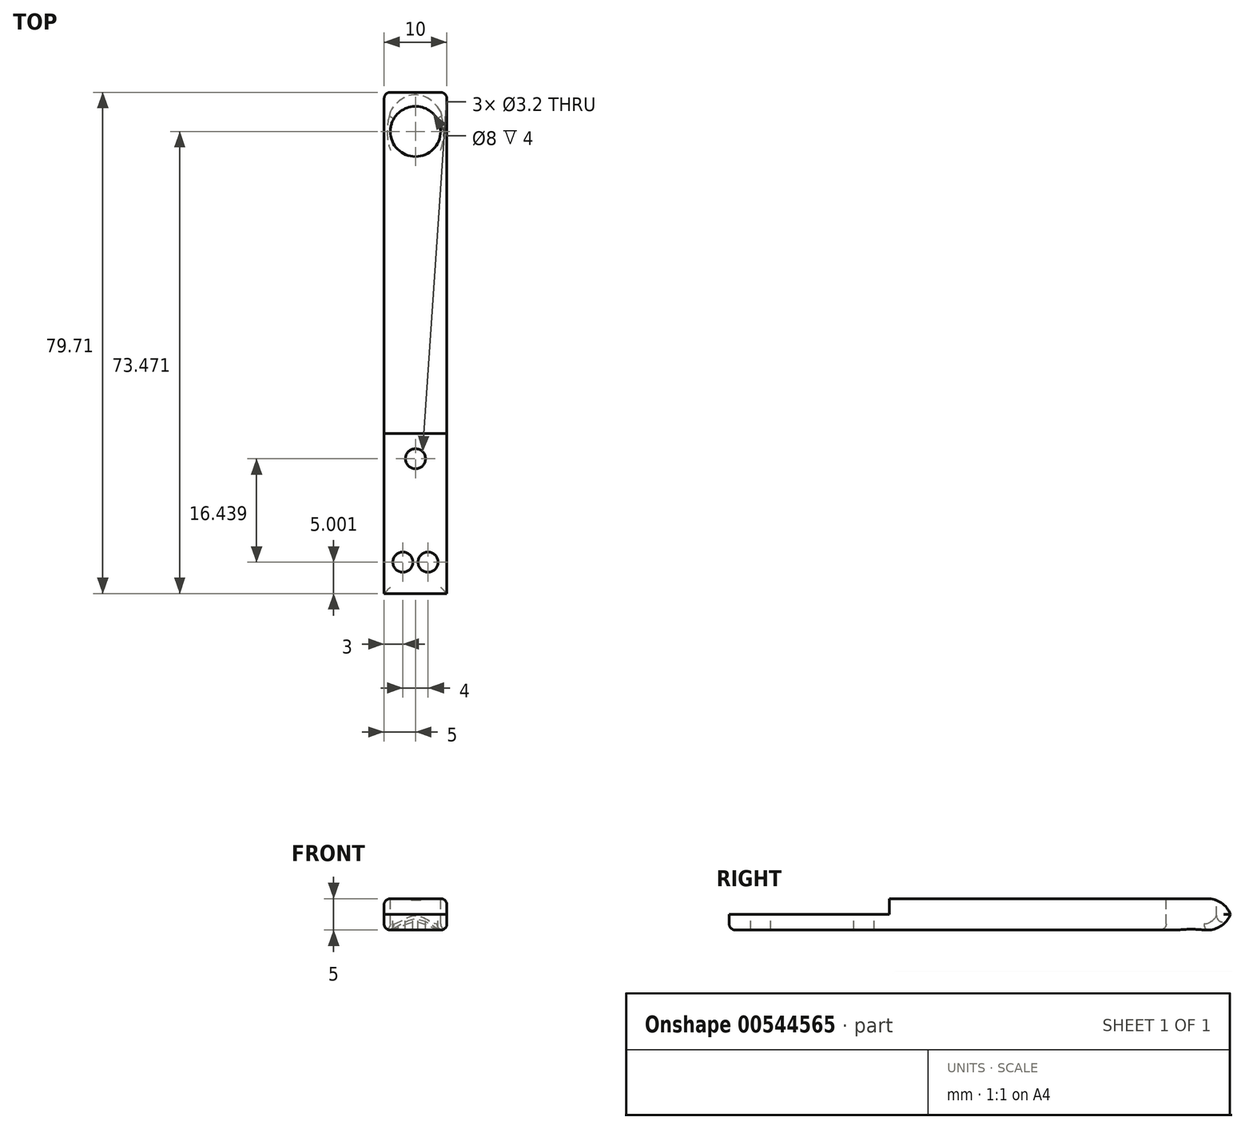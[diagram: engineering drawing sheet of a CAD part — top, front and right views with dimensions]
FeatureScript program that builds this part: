
annotation { "Feature Type Name" : "Feature", "Feature Type Description" : "" }
export const myFeature = defineFeature(function(context is Context, id is Id, definition is map)
    precondition{}
    {
        {
            var Q0;
            Q0=qCreatedBy(makeId("Top.planeOp"),FACE);
            var sketch = newSketch(context, id + "F0", { "sketchPlane" : qUnion([Q0])});
            skLineSegment(sketch, "E0", {"start": v(-5, 54.56) * mm, "end": v(5, 54.56) * mm});
            skLineSegment(sketch, "E1", {"start": v(5, 54.56) * mm, "end": v(5, -25.44) * mm});
            skLineSegment(sketch, "E2", {"start": v(5, -25.44) * mm, "end": v(-5, -25.44) * mm});
            skLineSegment(sketch, "E3", {"start": v(-5, -25.44) * mm, "end": v(-5, 54.56) * mm});
            skSolve(sketch);
        }
        {
            var Q0;
            Q0 = qSketchRegion(id + "F0", true);
            extrude(context, id + "F1", {"entities" : qUnion([Q0]), "depth" : 5 * mm, "offsetDistance" : 25 * mm});
        }
        {
            var Q0;
            Q0=makeQuery(id+"F1.opExtrude","CAP_FACE",FACE,{"disambiguationData":[OSD([sQuery(id+"F0.wireOp",EDGE,"E0"),sQuery(id+"F0.wireOp",EDGE,"E1"),sQuery(id+"F0.wireOp",EDGE,"E2"),sQuery(id+"F0.wireOp",EDGE,"E3")])],"isStart":false});
            var sketch = newSketch(context, id + "F2", { "sketchPlane" : qUnion([Q0])});
            skLineSegment(sketch, "E4.bottom", {"start": v(5, -25.44) * mm, "end": v(-5, -25.44) * mm});
            skLineSegment(sketch, "E4.top", {"start": v(5, -25.44) * mm, "end": v(-5, -25.44) * mm});
            skLineSegment(sketch, "E4.left", {"start": v(5, -25.44) * mm, "end": v(5, -25.44) * mm});
            skLineSegment(sketch, "E4.right", {"start": v(-5, -25.44) * mm, "end": v(-5, -25.44) * mm});
            skLineSegment(sketch, "E5.bottom", {"start": v(-5, -25.44) * mm, "end": v(5, -25.44) * mm});
            skLineSegment(sketch, "E5.top", {"start": v(-5, 0) * mm, "end": v(5, 0) * mm});
            skLineSegment(sketch, "E5.left", {"start": v(-5, -25.44) * mm, "end": v(-5, 0) * mm});
            skLineSegment(sketch, "E5.right", {"start": v(5, -25.44) * mm, "end": v(5, 0) * mm});
            skSolve(sketch);
        }
        {
            var Q0;
            Q0 = qSketchRegion(id + "F2", true);
            extrude(context, id + "F3", {"entities" : qUnion([Q0]), "operationType" : NewBodyOperationType.REMOVE, "oppositeDirection" : true, "depth" : 2.5 * mm, "offsetDistance" : 25 * mm});
        }
        {
            var Q0;
            Q0=makeQuery(id+"F3.boolean.opBoolean","COPY",FACE,{"derivedFrom":makeQuery(id+"F3.opExtrude","CAP_FACE",FACE,{"disambiguationData":[OSD([sQuery(id+"F2.wireOp",EDGE,"E5.bottom"),sQuery(id+"F2.wireOp",EDGE,"E5.top"),sQuery(id+"F2.wireOp",EDGE,"E5.left"),sQuery(id+"F2.wireOp",EDGE,"E5.right")])],"isStart":false})});
            var sketch = newSketch(context, id + "F4", { "sketchPlane" : qUnion([Q0])});
            skCircle(sketch, "E6", {"center": v(2, -20.44) * mm, "radius": 1.6 * mm});
            skCircle(sketch, "E7", {"center": v(-2, -20.44) * mm, "radius": 1.6 * mm});
            skCircle(sketch, "E8", {"center": v(0, -4) * mm, "radius": 1.6 * mm});
            skSolve(sketch);
        }
        {
            var Q0;
            Q0 = qSketchRegion(id + "F4", true);
            extrude(context, id + "F5", {"entities" : qUnion([Q0]), "operationType" : NewBodyOperationType.REMOVE, "oppositeDirection" : true, "depth" : 25 * mm, "offsetDistance" : 25 * mm});
        }
        {
            var Q0;
            {var subQ0=sQuery(id+"F2.wireOp",EDGE,"E5.top");Q0=makeQuery(id+"F2.imprint","IMPRINT",FACE,{"disambiguationData":[TD([[makeQuery(id+"F2.imprint","IMPRINT",EDGE,{"derivedFrom":subQ0}),1.0]])]});}
            var sketch = newSketch(context, id + "F6", { "sketchPlane" : qUnion([Q0])});
            skCircle(sketch, "E9", {"center": v(0, 48.03) * mm, "radius": 4 * mm});
            skSolve(sketch);
        }
        {
            var Q0;
            Q0 = qSketchRegion(id + "F6", true);
            extrude(context, id + "F7", {"entities" : qUnion([Q0]), "operationType" : NewBodyOperationType.REMOVE, "oppositeDirection" : true, "depth" : 25 * mm, "offsetDistance" : 25 * mm});
        }
        {
            var Q0;
            Q0=makeQuery(id+"F1.opExtrude","CAP_EDGE",EDGE,{"disambiguationData":[OSD([sQuery(id+"F0.wireOp",EDGE,"E0")])],"isStart":false});
            var Q1;
            Q1=makeQuery(id+"F1.opExtrude","CAP_EDGE",EDGE,{"disambiguationData":[OSD([sQuery(id+"F0.wireOp",EDGE,"E0")])],"isStart":true});
            fillet(context, id + "F8", {"entities" : qUnion([Q0, Q1]), "radius" : 4 * mm, "tangentPropagation" : true, "allowEdgeOverflow" : false});
        }
        {
            var Q0;
            Q0=makeQuery(id+"F7.boolean.opBoolean","INTERSECT",EDGE,{"derivedFrom":[makeQuery(id+"F1.opExtrude","CAP_FACE",FACE,{"disambiguationData":[OSD([sQuery(id+"F0.wireOp",EDGE,"E0"),sQuery(id+"F0.wireOp",EDGE,"E1"),sQuery(id+"F0.wireOp",EDGE,"E2"),sQuery(id+"F0.wireOp",EDGE,"E3")])],"isStart":true}),makeQuery(id+"F7.opExtrude","SWEPT_FACE",FACE,{"disambiguationData":[OSD([sQuery(id+"F6.wireOp",EDGE,"E9")])]})]});
            var Q1;
            Q1=makeQuery(id+"F7.boolean.opBoolean","COPY",EDGE,{"derivedFrom":makeQuery(id+"F7.opExtrude","CAP_EDGE",EDGE,{"disambiguationData":[OSD([sQuery(id+"F6.wireOp",EDGE,"E9")])],"isStart":true})});
            var Q2;
            Q2=makeQuery(id+"F1.opExtrude","CAP_EDGE",EDGE,{"disambiguationData":[OSD([sQuery(id+"F0.wireOp",EDGE,"E3")])],"isStart":false});
            var Q3;
            Q3=makeQuery(id+"F1.opExtrude","CAP_EDGE",EDGE,{"disambiguationData":[OSD([sQuery(id+"F0.wireOp",EDGE,"E1")])],"isStart":false});
            var Q4;
            Q4=makeQuery(id+"F1.opExtrude","CAP_EDGE",EDGE,{"disambiguationData":[OSD([sQuery(id+"F0.wireOp",EDGE,"E1")])],"isStart":true});
            var Q5;
            Q5=makeQuery(id+"F1.opExtrude","CAP_EDGE",EDGE,{"disambiguationData":[OSD([sQuery(id+"F0.wireOp",EDGE,"E3")])],"isStart":true});
            var Q6;
            Q6=makeQuery(id+"F1.opExtrude","CAP_EDGE",EDGE,{"disambiguationData":[OSD([sQuery(id+"F0.wireOp",EDGE,"E2")])],"isStart":true});
            fillet(context, id + "F9", {"entities" : qUnion([Q0, Q1, Q2, Q3, Q4, Q5, Q6]), "radius" : 1 * mm, "tangentPropagation" : true, "allowEdgeOverflow" : false});
        }
    });
